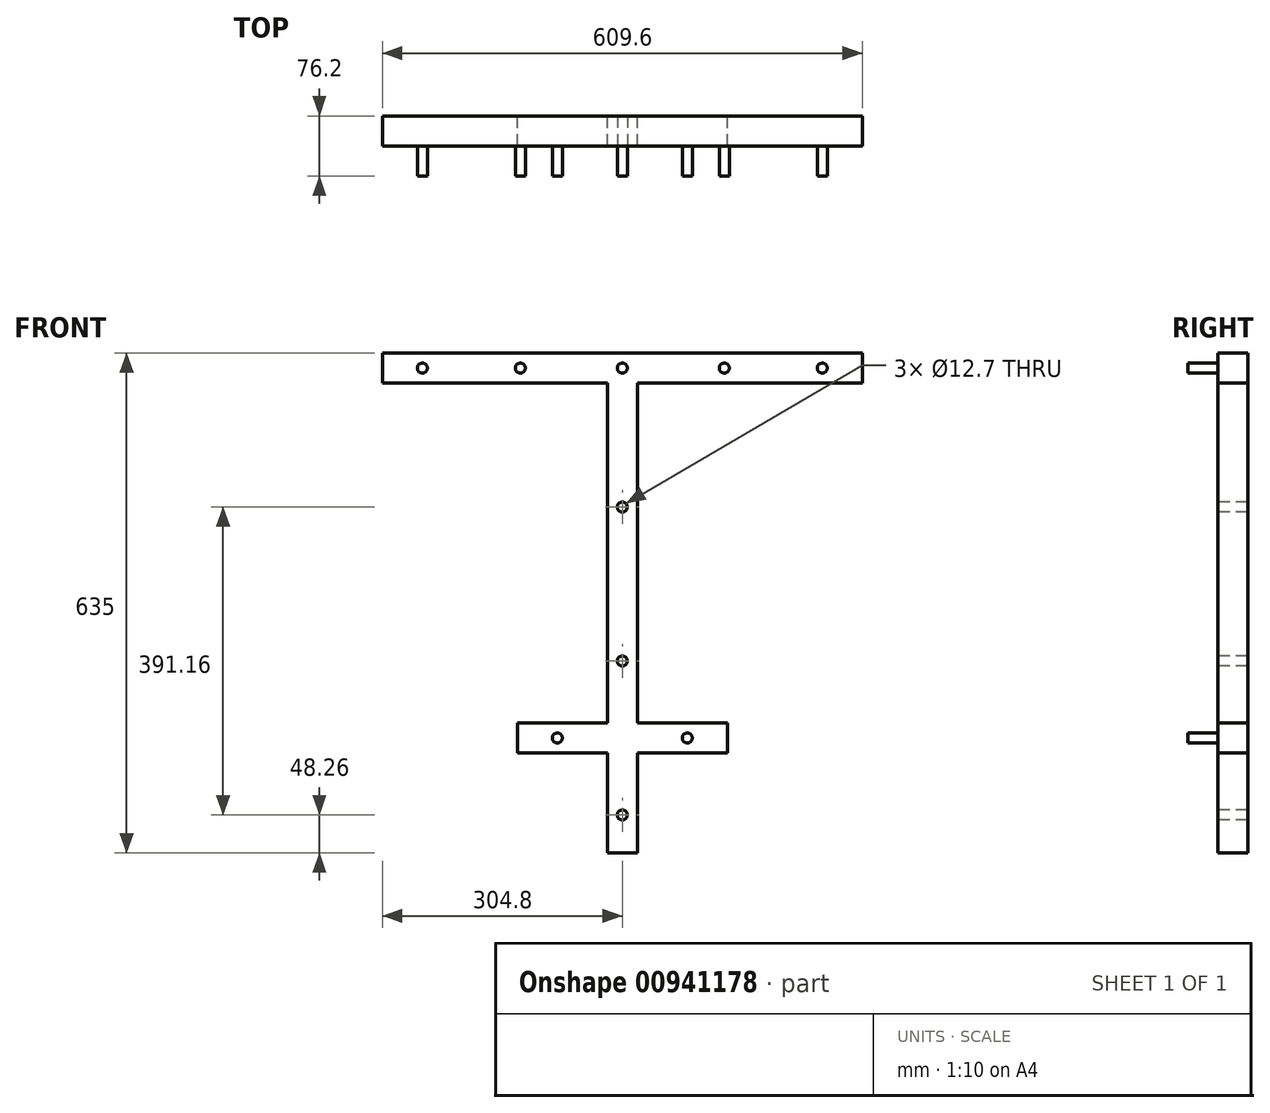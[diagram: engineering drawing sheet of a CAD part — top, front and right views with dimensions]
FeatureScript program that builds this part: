
annotation { "Feature Type Name" : "Feature", "Feature Type Description" : "" }
export const myFeature = defineFeature(function(context is Context, id is Id, definition is map)
    precondition{}
    {
        {
            var Q0;
            Q0=qCreatedBy(makeId("Front.planeOp"),FACE);
            var sketch = newSketch(context, id + "F0", { "sketchPlane" : qUnion([Q0])});
            skLineSegment(sketch, "E0.bottom", {"start": v(-285.75, 635) * mm, "end": v(323.85, 635) * mm});
            skLineSegment(sketch, "E0.top", {"start": v(-285.75, 596.9) * mm, "end": v(0, 596.9) * mm});
            skLineSegment(sketch, "E0.left", {"start": v(-285.75, 635) * mm, "end": v(-285.75, 596.9) * mm});
            skLineSegment(sketch, "E0.right", {"start": v(323.85, 635) * mm, "end": v(323.85, 596.9) * mm});
            skLineSegment(sketch, "E1.top", {"start": v(0, 0) * mm, "end": v(38.1, 0) * mm});
            skLineSegment(sketch, "E1.left", {"start": v(0, 596.9) * mm, "end": v(0, 165.1) * mm});
            skLineSegment(sketch, "E1.right", {"start": v(38.1, 596.9) * mm, "end": v(38.1, 165.1) * mm});
            skLineSegment(sketch, "E2.trimOffspring", {"start": v(38.1, 596.9) * mm, "end": v(323.85, 596.9) * mm});
            skLineSegment(sketch, "E3.bottom", {"start": v(-114.3, 165.1) * mm, "end": v(0, 165.1) * mm});
            skLineSegment(sketch, "E3.top", {"start": v(-114.3, 127) * mm, "end": v(0, 127) * mm});
            skLineSegment(sketch, "E3.left", {"start": v(-114.3, 165.1) * mm, "end": v(-114.3, 127) * mm});
            skLineSegment(sketch, "E3.right", {"start": v(152.4, 165.1) * mm, "end": v(152.4, 127) * mm});
            skLineSegment(sketch, "E4", {"start": v(-479.69, -635) * mm, "end": v(527.11, -635) * mm, "construction": true});
            skLineSegment(sketch, "E5.trimOffspring", {"start": v(38.1, 165.1) * mm, "end": v(152.4, 165.1) * mm});
            skLineSegment(sketch, "E6.trimOffspring", {"start": v(0, 127) * mm, "end": v(0, 0) * mm});
            skLineSegment(sketch, "E7.trimOffspring", {"start": v(38.1, 127) * mm, "end": v(152.4, 127) * mm});
            skLineSegment(sketch, "E8.trimOffspring", {"start": v(38.1, 127) * mm, "end": v(38.1, 0) * mm});
            skSolve(sketch);
        }
        {
            var Q0;
            Q0 = qSketchRegion(id + "F0", true);
            extrude(context, id + "F1", {"entities" : qUnion([Q0]), "depth" : 38.1 * mm, "offsetDistance" : 25.4 * mm});
        }
        {
            var Q0;
            Q0 = qSketchRegion(id + "F0", true);
            extrude(context, id + "F2", {"entities" : qUnion([Q0]), "operationType" : NewBodyOperationType.ADD, "depth" : 38.1 * mm, "offsetDistance" : 25.4 * mm});
        }
        {
            var Q0;
            Q0=makeQuery(id+"F1.opExtrude","CAP_FACE",FACE,{"disambiguationData":[OSD([sQuery(id+"F0.wireOp",EDGE,"E0.bottom"),sQuery(id+"F0.wireOp",EDGE,"E0.top"),sQuery(id+"F0.wireOp",EDGE,"E0.left"),sQuery(id+"F0.wireOp",EDGE,"E0.right"),sQuery(id+"F0.wireOp",EDGE,"E1.top"),sQuery(id+"F0.wireOp",EDGE,"E1.left"),sQuery(id+"F0.wireOp",EDGE,"E1.right"),sQuery(id+"F0.wireOp",EDGE,"E2.trimOffspring"),sQuery(id+"F0.wireOp",EDGE,"E3.bottom"),sQuery(id+"F0.wireOp",EDGE,"E3.top"),sQuery(id+"F0.wireOp",EDGE,"E3.left"),sQuery(id+"F0.wireOp",EDGE,"E3.right"),sQuery(id+"F0.wireOp",EDGE,"E5.trimOffspring"),sQuery(id+"F0.wireOp",EDGE,"E6.trimOffspring"),sQuery(id+"F0.wireOp",EDGE,"E7.trimOffspring"),sQuery(id+"F0.wireOp",EDGE,"E8.trimOffspring")])],"isStart":false});
            var sketch = newSketch(context, id + "F3", { "sketchPlane" : qUnion([Q0])});
            skLineSegment(sketch, "E9", {"start": v(-234.95, 729.5) * mm, "end": v(-234.95, 487.66) * mm, "construction": true});
            skLineSegment(sketch, "E10", {"start": v(-285.75, 754.73) * mm, "end": v(-285.75, 475.04) * mm, "construction": true});
            skLineSegment(sketch, "E11", {"start": v(-110.5, 729.5) * mm, "end": v(-110.5, 483.45) * mm, "construction": true});
            skLineSegment(sketch, "E12", {"start": v(19.05, 735.8) * mm, "end": v(19.05, 466.63) * mm, "construction": true});
            skLineSegment(sketch, "E13", {"start": v(148.59, 756.83) * mm, "end": v(148.59, 409.85) * mm, "construction": true});
            skLineSegment(sketch, "E14", {"start": v(273.05, 803.24) * mm, "end": v(273.05, 428.63) * mm, "construction": true});
            skLineSegment(sketch, "E15", {"start": v(323.85, 866.18) * mm, "end": v(323.85, 483.45) * mm, "construction": true});
            skLineSegment(sketch, "E16", {"start": v(152.4, 279.47) * mm, "end": v(152.4, 35.53) * mm, "construction": true});
            skLineSegment(sketch, "E17", {"start": v(-114.3, 266.86) * mm, "end": v(-114.3, -23.36) * mm, "construction": true});
            skLineSegment(sketch, "E18", {"start": v(-63.5, 266.96) * mm, "end": v(-63.5, -15.44) * mm, "construction": true});
            skLineSegment(sketch, "E19", {"start": v(101.6, 258.3) * mm, "end": v(101.6, 15.72) * mm, "construction": true});
            skLineSegment(sketch, "E20", {"start": v(-369.32, 615.95) * mm, "end": v(506.29, 615.95) * mm, "construction": true});
            skLineSegment(sketch, "E21", {"start": v(-218.05, 146.05) * mm, "end": v(323.85, 146.05) * mm, "construction": true});
            skCircle(sketch, "E22", {"center": v(-234.95, 615.95) * mm, "radius": 6.35 * mm});
            skCircle(sketch, "E23", {"center": v(-110.5, 615.95) * mm, "radius": 6.35 * mm});
            skCircle(sketch, "E24", {"center": v(19.05, 615.95) * mm, "radius": 6.35 * mm});
            skCircle(sketch, "E25", {"center": v(148.59, 615.95) * mm, "radius": 6.35 * mm});
            skCircle(sketch, "E26", {"center": v(273.05, 615.94) * mm, "radius": 6.35 * mm});
            skCircle(sketch, "E27", {"center": v(-63.5, 146.05) * mm, "radius": 6.35 * mm});
            skCircle(sketch, "E28", {"center": v(101.6, 146.05) * mm, "radius": 6.35 * mm});
            skSolve(sketch);
        }
        {
            var Q0;
            Q0 = qSketchRegion(id + "F3", true);
            extrude(context, id + "F4", {"entities" : qUnion([Q0]), "operationType" : NewBodyOperationType.ADD, "depth" : 38.1 * mm, "offsetDistance" : 25.4 * mm});
        }
        {
            var Q0;
            Q0=makeQuery(id+"F1.opExtrude","CAP_FACE",FACE,{"disambiguationData":[OSD([sQuery(id+"F0.wireOp",EDGE,"E0.bottom"),sQuery(id+"F0.wireOp",EDGE,"E0.top"),sQuery(id+"F0.wireOp",EDGE,"E0.left"),sQuery(id+"F0.wireOp",EDGE,"E0.right"),sQuery(id+"F0.wireOp",EDGE,"E1.top"),sQuery(id+"F0.wireOp",EDGE,"E1.left"),sQuery(id+"F0.wireOp",EDGE,"E1.right"),sQuery(id+"F0.wireOp",EDGE,"E2.trimOffspring"),sQuery(id+"F0.wireOp",EDGE,"E3.bottom"),sQuery(id+"F0.wireOp",EDGE,"E3.top"),sQuery(id+"F0.wireOp",EDGE,"E3.left"),sQuery(id+"F0.wireOp",EDGE,"E3.right"),sQuery(id+"F0.wireOp",EDGE,"E5.trimOffspring"),sQuery(id+"F0.wireOp",EDGE,"E6.trimOffspring"),sQuery(id+"F0.wireOp",EDGE,"E7.trimOffspring"),sQuery(id+"F0.wireOp",EDGE,"E8.trimOffspring")])],"isStart":false});
            var sketch = newSketch(context, id + "F5", { "sketchPlane" : qUnion([Q0])});
            skLineSegment(sketch, "E29", {"start": v(19.05, 0) * mm, "end": v(19.05, 657.95) * mm, "construction": true});
            skCircle(sketch, "E30", {"center": v(19.05, 439.42) * mm, "radius": 6.35 * mm});
            skCircle(sketch, "E31", {"center": v(19.05, 243.84) * mm, "radius": 6.35 * mm});
            skCircle(sketch, "E32", {"center": v(19.05, 48.26) * mm, "radius": 6.35 * mm});
            skSolve(sketch);
        }
        {
            var Q0;
            Q0 = qSketchRegion(id + "F5", true);
            extrude(context, id + "F6", {"entities" : qUnion([Q0]), "operationType" : NewBodyOperationType.REMOVE, "oppositeDirection" : true, "depth" : 38.1 * mm, "offsetDistance" : 25.4 * mm});
        }
    });
